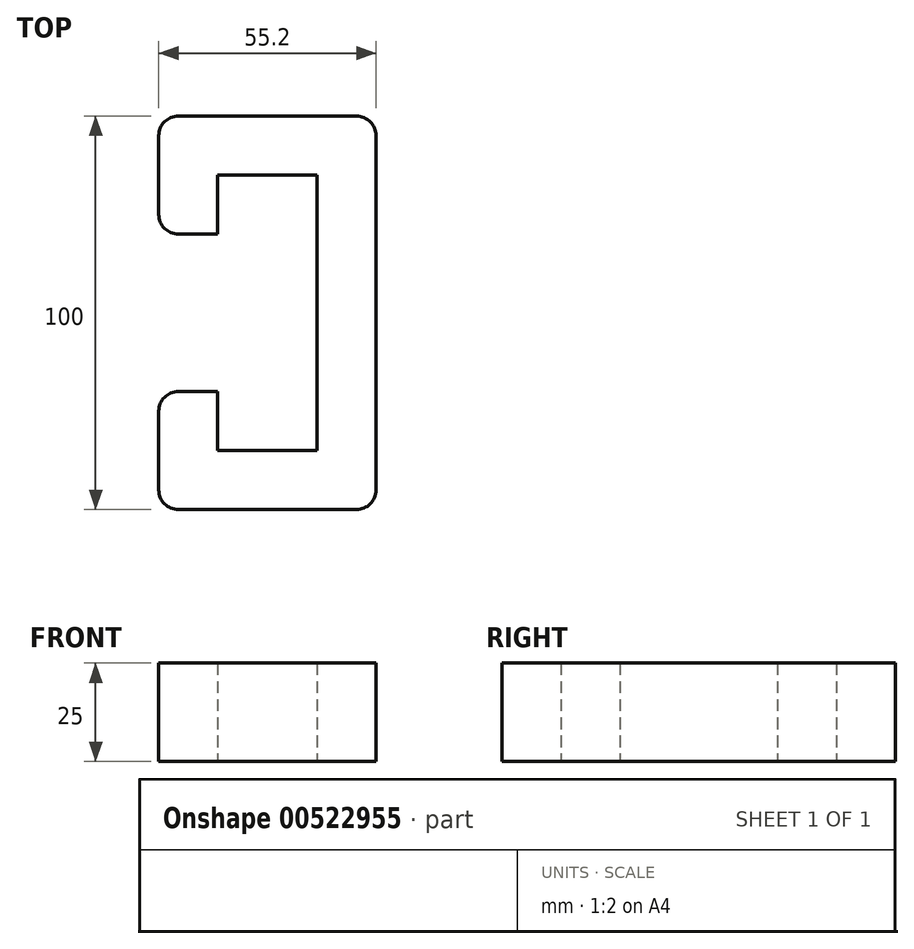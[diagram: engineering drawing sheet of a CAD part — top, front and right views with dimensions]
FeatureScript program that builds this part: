
annotation { "Feature Type Name" : "Feature", "Feature Type Description" : "" }
export const myFeature = defineFeature(function(context is Context, id is Id, definition is map)
    precondition{}
    {
        {
            var Q0;
            Q0=qCreatedBy(makeId("Top.planeOp"),FACE);
            var sketch = newSketch(context, id + "F0", { "sketchPlane" : qUnion([Q0])});
            skLineSegment(sketch, "E0", {"start": v(0, 0) * mm, "end": v(0, 35) * mm});
            skLineSegment(sketch, "E1", {"start": v(0, 35) * mm, "end": v(-25.2, 35) * mm});
            skLineSegment(sketch, "E2", {"start": v(-25.2, 35) * mm, "end": v(-25.2, 20) * mm});
            skLineSegment(sketch, "E3.MirrorCS", {"start": v(0, 0) * mm, "end": v(0, -35) * mm});
            skLineSegment(sketch, "E4.MirrorCS", {"start": v(0, -35) * mm, "end": v(-25.2, -35) * mm});
            skLineSegment(sketch, "E5.MirrorCS", {"start": v(-25.2, -35) * mm, "end": v(-25.2, -20) * mm});
            skLineSegment(sketch, "E6.0", {"start": v(-40.2, -45) * mm, "end": v(-40.2, -25) * mm});
            skLineSegment(sketch, "E6.1", {"start": v(10, -50) * mm, "end": v(-35.2, -50) * mm});
            skLineSegment(sketch, "E6.2", {"start": v(-40.2, 45) * mm, "end": v(-40.2, 25) * mm});
            skLineSegment(sketch, "E6.3", {"start": v(10, 50) * mm, "end": v(-35.2, 50) * mm});
            skLineSegment(sketch, "E6.4", {"start": v(15, 0) * mm, "end": v(15, 45) * mm});
            skLineSegment(sketch, "E6.5", {"start": v(15, 0) * mm, "end": v(15, -45) * mm});
            skLineSegment(sketch, "E7", {"start": v(-25.2, -20) * mm, "end": v(-35.2, -20) * mm});
            skLineSegment(sketch, "E8", {"start": v(-25.2, 20) * mm, "end": v(-35.2, 20) * mm});
            skPoint(sketch, "E9.visualSharp", {"position": v(-40.2, 50) * mm});
            skArc(sketch, "E9.filletArc", {"start": v(-35.2, 50) * mm, "mid": v(-38.74, 48.54) * mm, "end": v(-40.2, 45) * mm});
            skPoint(sketch, "E10.visualSharp", {"position": v(15, 50) * mm});
            skArc(sketch, "E10.filletArc", {"start": v(15, 45) * mm, "mid": v(13.54, 48.54) * mm, "end": v(10, 50) * mm});
            skPoint(sketch, "E11.visualSharp", {"position": v(15, -50) * mm});
            skArc(sketch, "E11.filletArc", {"start": v(10, -50) * mm, "mid": v(13.54, -48.54) * mm, "end": v(15, -45) * mm});
            skPoint(sketch, "E12.visualSharp", {"position": v(-40.2, -50) * mm});
            skArc(sketch, "E12.filletArc", {"start": v(-40.2, -45) * mm, "mid": v(-38.74, -48.54) * mm, "end": v(-35.2, -50) * mm});
            skPoint(sketch, "E13.visualSharp", {"position": v(-40.2, -20) * mm});
            skArc(sketch, "E13.filletArc", {"start": v(-35.2, -20) * mm, "mid": v(-38.74, -21.46) * mm, "end": v(-40.2, -25) * mm});
            skPoint(sketch, "E14.visualSharp", {"position": v(-40.2, 20) * mm});
            skArc(sketch, "E14.filletArc", {"start": v(-40.2, 25) * mm, "mid": v(-38.74, 21.46) * mm, "end": v(-35.2, 20) * mm});
            skSolve(sketch);
        }
        {
            var Q0;
            Q0 = qSketchRegion(id + "F0", true);
            extrude(context, id + "F1", {"entities" : qUnion([Q0]), "depth" : 25 * mm, "offsetDistance" : 25 * mm});
        }
    });
